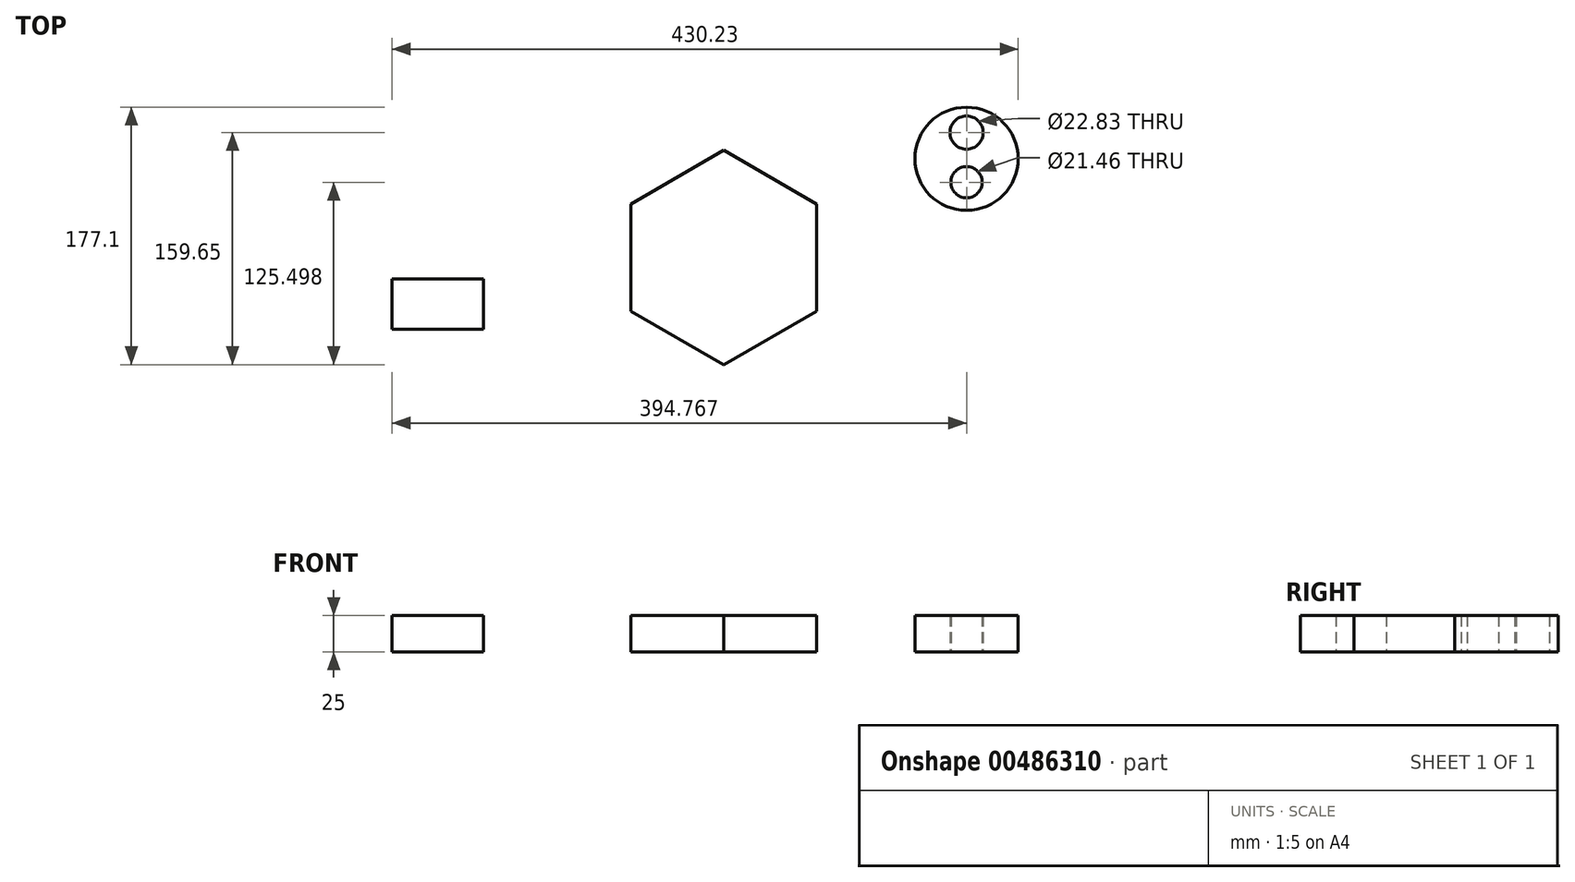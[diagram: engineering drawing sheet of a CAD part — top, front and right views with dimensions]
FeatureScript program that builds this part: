
annotation { "Feature Type Name" : "Feature", "Feature Type Description" : "" }
export const myFeature = defineFeature(function(context is Context, id is Id, definition is map)
    precondition{}
    {
        {
            var Q0;
            Q0=qCreatedBy(makeId("Top.planeOp"),FACE);
            var sketch = newSketch(context, id + "F0", { "sketchPlane" : qUnion([Q0])});
            skCircle(sketch, "E0.cCircle", {"center": v(0, 0) * mm, "radius": 63.84 * mm, "construction": true});
            skLineSegment(sketch, "E0.0", {"start": v(63.84, 36.86) * mm, "end": v(63.84, -36.86) * mm});
            skLineSegment(sketch, "E0.1", {"start": v(63.84, -36.86) * mm, "end": v(0, -73.72) * mm});
            skLineSegment(sketch, "E0.2", {"start": v(0, -73.72) * mm, "end": v(-63.84, -36.86) * mm});
            skLineSegment(sketch, "E0.3", {"start": v(-63.84, -36.86) * mm, "end": v(-63.84, 36.86) * mm});
            skLineSegment(sketch, "E0.4", {"start": v(-63.84, 36.86) * mm, "end": v(0, 73.72) * mm});
            skLineSegment(sketch, "E0.5", {"start": v(0, 73.72) * mm, "end": v(63.84, 36.86) * mm});
            skPoint(sketch, "E0.0.midPoint", {"position": v(63.84, 0) * mm});
            skSolve(sketch);
        }
        {
            var Q0;
            Q0=makeQuery(id+"F0.imprint","IMPRINT",FACE,{"disambiguationData":[TD([[makeQuery(id+"F0.imprint","IMPRINT",EDGE,{"derivedFrom":sQuery(id+"F0.wireOp",EDGE,"E0.0")}),-1.0]])]});
            extrude(context, id + "F1", {"entities" : qUnion([Q0]), "depth" : 25 * mm});
        }
        {
            var Q0;
            Q0=qCreatedBy(makeId("Top.planeOp"),FACE);
            var sketch = newSketch(context, id + "F2", { "sketchPlane" : qUnion([Q0])});
            skCircle(sketch, "E1", {"center": v(166.98, 67.92) * mm, "radius": 35.46 * mm});
            skCircle(sketch, "E2", {"center": v(166.98, 85.93) * mm, "radius": 11.41 * mm});
            skCircle(sketch, "E3", {"center": v(166.98, 51.78) * mm, "radius": 10.73 * mm});
            skSolve(sketch);
        }
        {
            var Q0;
            Q0=makeQuery(id+"F2.imprint","IMPRINT",FACE,{"disambiguationData":[TD([[makeQuery(id+"F2.imprint","IMPRINT",EDGE,{"derivedFrom":sQuery(id+"F2.wireOp",EDGE,"E1")}),1.0]])]});
            extrude(context, id + "F3", {"entities" : qUnion([Q0]), "depth" : 25 * mm});
        }
        {
            var Q0;
            Q0=qCreatedBy(makeId("Top.planeOp"),FACE);
            var sketch = newSketch(context, id + "F4", { "sketchPlane" : qUnion([Q0])});
            skLineSegment(sketch, "E4.bottom", {"start": v(-164.9, -14.73) * mm, "end": v(-227.8, -14.73) * mm});
            skLineSegment(sketch, "E4.top", {"start": v(-164.9, -49.4) * mm, "end": v(-227.8, -49.4) * mm});
            skLineSegment(sketch, "E4.left", {"start": v(-164.9, -14.73) * mm, "end": v(-164.9, -49.4) * mm});
            skLineSegment(sketch, "E4.right", {"start": v(-227.8, -14.73) * mm, "end": v(-227.8, -49.4) * mm});
            skPoint(sketch, "E4.middle", {"position": v(-196.35, -32.06) * mm});
            skSolve(sketch);
        }
        {
            var Q0;
            Q0=makeQuery(id+"F4.imprint","IMPRINT",FACE,{"disambiguationData":[TD([[makeQuery(id+"F4.imprint","IMPRINT",EDGE,{"derivedFrom":sQuery(id+"F4.wireOp",EDGE,"E4.bottom")}),1.0]])]});
            extrude(context, id + "F5", {"entities" : qUnion([Q0]), "depth" : 25 * mm});
        }
    });
